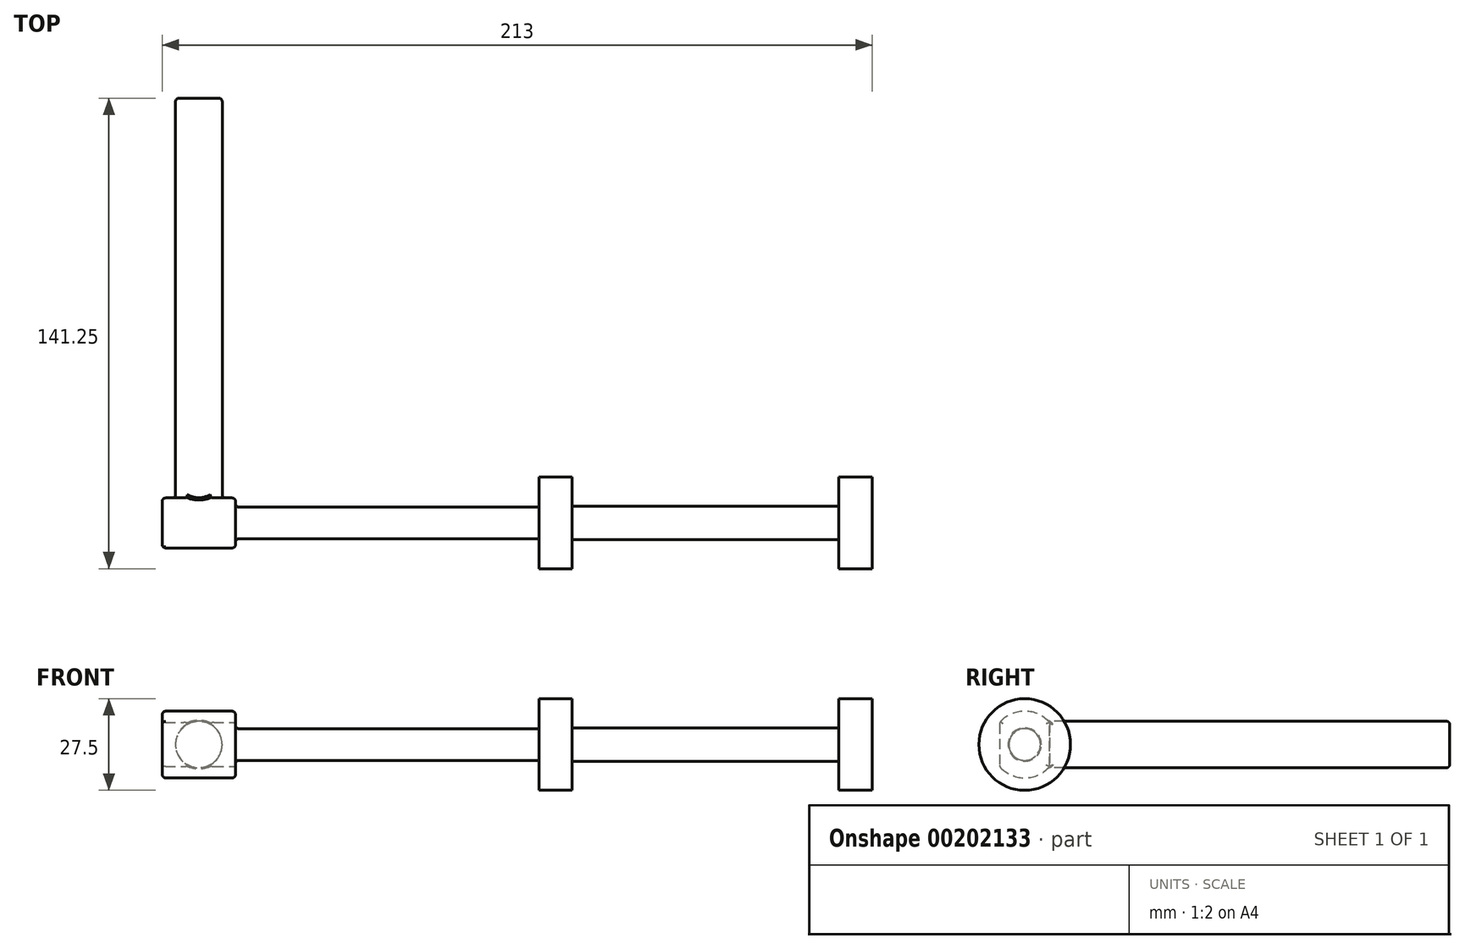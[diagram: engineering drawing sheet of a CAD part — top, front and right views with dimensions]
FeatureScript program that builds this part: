
annotation { "Feature Type Name" : "Feature", "Feature Type Description" : "" }
export const myFeature = defineFeature(function(context is Context, id is Id, definition is map)
    precondition{}
    {
        {
            var Q0;
            Q0=qCreatedBy(makeId("Front.planeOp"),FACE);
            var sketch = newSketch(context, id + "F0", { "sketchPlane" : qUnion([Q0])});
            skLineSegment(sketch, "E0", {"start": v(-50, 13.75) * mm, "end": v(-50, 0) * mm});
            skLineSegment(sketch, "E1", {"start": v(-50, 0) * mm, "end": v(0, 0) * mm});
            skLineSegment(sketch, "E2", {"start": v(0, 0) * mm, "end": v(0, 5) * mm});
            skLineSegment(sketch, "E3", {"start": v(0, 5) * mm, "end": v(-40, 5) * mm});
            skLineSegment(sketch, "E4", {"start": v(-40, 5) * mm, "end": v(-40, 13.75) * mm});
            skLineSegment(sketch, "E5", {"start": v(-40, 13.75) * mm, "end": v(-50, 13.75) * mm});
            skLineSegment(sketch, "E6.MirrorCS", {"start": v(40, 13.75) * mm, "end": v(50, 13.75) * mm});
            skLineSegment(sketch, "E7.MirrorCS", {"start": v(50, 13.75) * mm, "end": v(50, 0) * mm});
            skLineSegment(sketch, "E8.MirrorCS", {"start": v(40, 5) * mm, "end": v(40, 13.75) * mm});
            skLineSegment(sketch, "E9.MirrorCS", {"start": v(0, 5) * mm, "end": v(40, 5) * mm});
            skLineSegment(sketch, "E10.MirrorCS", {"start": v(50, 0) * mm, "end": v(0, 0) * mm});
            skLineSegment(sketch, "E11.bottom", {"start": v(-50, 0) * mm, "end": v(-141, 0) * mm});
            skLineSegment(sketch, "E11.top", {"start": v(-50, 4.75) * mm, "end": v(-141, 4.75) * mm});
            skLineSegment(sketch, "E11.left", {"start": v(-50, 0) * mm, "end": v(-50, 4.75) * mm});
            skLineSegment(sketch, "E11.right", {"start": v(-141, 0) * mm, "end": v(-141, 4.75) * mm});
            skSolve(sketch);
        }
        {
            var Q0;
            Q0 = qSketchRegion(id + "F0", true);
            var Q1;
            Q1=sQuery(id+"F0.wireOp",EDGE,"E10.MirrorCS");
            revolve(context, id + "F1", {"entities" : qUnion([Q0]), "axis" : qUnion([Q1]), "revolveType" : RevolveType.FULL});
        }
        {
            var Q0;
            Q0=makeQuery(id+"F1.opRevolve","SWEPT_FACE",FACE,{"disambiguationData":[OSD([sQuery(id+"F0.wireOp",EDGE,"E11.right")])]});
            var sketch = newSketch(context, id + "F2", { "sketchPlane" : qUnion([Q0])});
            skLineSegment(sketch, "E12.bottom", {"start": v(-7.5, 6.61) * mm, "end": v(7.5, 6.61) * mm});
            skLineSegment(sketch, "E12.top", {"start": v(-7.5, -6.61) * mm, "end": v(7.5, -6.61) * mm});
            skLineSegment(sketch, "E12.left", {"start": v(-7.5, 6.61) * mm, "end": v(-7.5, -6.61) * mm});
            skLineSegment(sketch, "E12.right", {"start": v(7.5, 6.61) * mm, "end": v(7.5, -6.61) * mm});
            skArc(sketch, "E13", {"start": v(7.5, 6.61) * mm, "mid": v(0, 10) * mm, "end": v(-7.5, 6.61) * mm});
            skArc(sketch, "E14.MirrorCS", {"start": v(7.5, -6.61) * mm, "mid": v(0, -10) * mm, "end": v(-7.5, -6.61) * mm});
            skSolve(sketch);
        }
        {
            var Q0;
            Q0 = qSketchRegion(id + "F2", true);
            extrude(context, id + "F3", {"entities" : qUnion([Q0]), "operationType" : NewBodyOperationType.ADD, "depth" : 22 * mm});
        }
        {
            var Q0;
            Q0=makeQuery(id+"F3.opExtrude","SWEPT_FACE",FACE,{"disambiguationData":[OSD([sQuery(id+"F2.wireOp",EDGE,"E12.left")])]});
            var sketch = newSketch(context, id + "F4", { "sketchPlane" : qUnion([Q0])});
            skCircle(sketch, "E15", {"center": v(152, 0) * mm, "radius": 7 * mm});
            skSolve(sketch);
        }
        {
            var Q0;
            Q0 = qSketchRegion(id + "F4", true);
            extrude(context, id + "F5", {"entities" : qUnion([Q0]), "operationType" : NewBodyOperationType.ADD, "depth" : 120 * mm});
        }
        {
            var Q0;
            Q0=makeQuery(id+"F3.opExtrude","CAP_FACE",FACE,{"disambiguationData":[OSD([sQuery(id+"F2.wireOp",EDGE,"E12.left"),sQuery(id+"F2.wireOp",EDGE,"E12.right"),sQuery(id+"F2.wireOp",EDGE,"E13"),sQuery(id+"F2.wireOp",EDGE,"E14.MirrorCS")])],"isStart":false});
            var Q1;
            Q1=makeQuery(id+"F3.opExtrude","CAP_FACE",FACE,{"disambiguationData":[OSD([sQuery(id+"F2.wireOp",EDGE,"E12.left"),sQuery(id+"F2.wireOp",EDGE,"E12.right"),sQuery(id+"F2.wireOp",EDGE,"E13"),sQuery(id+"F2.wireOp",EDGE,"E14.MirrorCS")])],"isStart":true});
            var Q2;
            Q2=makeQuery(id+"F5.opExtrude","CAP_EDGE",EDGE,{"disambiguationData":[OSD([sQuery(id+"F4.wireOp",EDGE,"E15")])],"isStart":false});
            var Q3;
            Q3=makeQuery(id+"F5.opExtrude","SWEPT_FACE",FACE,{"disambiguationData":[OSD([sQuery(id+"F4.wireOp",EDGE,"E15")])]});
            var Q4;
            Q4=makeQuery(id+"F3.opExtrude","SWEPT_EDGE",EDGE,{"disambiguationData":[OSD([sQuery(id+"F2.wireOp",EDGE,"E12.bottom"),sQuery(id+"F2.wireOp",EDGE,"E12.right"),sQuery(id+"F2.wireOp",EDGE,"E13")])]});
            var Q5;
            Q5=makeQuery(id+"F3.opExtrude","SWEPT_EDGE",EDGE,{"disambiguationData":[OSD([sQuery(id+"F2.wireOp",EDGE,"E12.top"),sQuery(id+"F2.wireOp",EDGE,"E12.right"),sQuery(id+"F2.wireOp",EDGE,"E14.MirrorCS")])]});
            fillet(context, id + "F6", {"entities" : qUnion([Q0, Q1, Q2, Q3, Q4, Q5]), "radius" : 1 * mm, "tangentPropagation" : true, "allowEdgeOverflow" : false});
        }
    });
